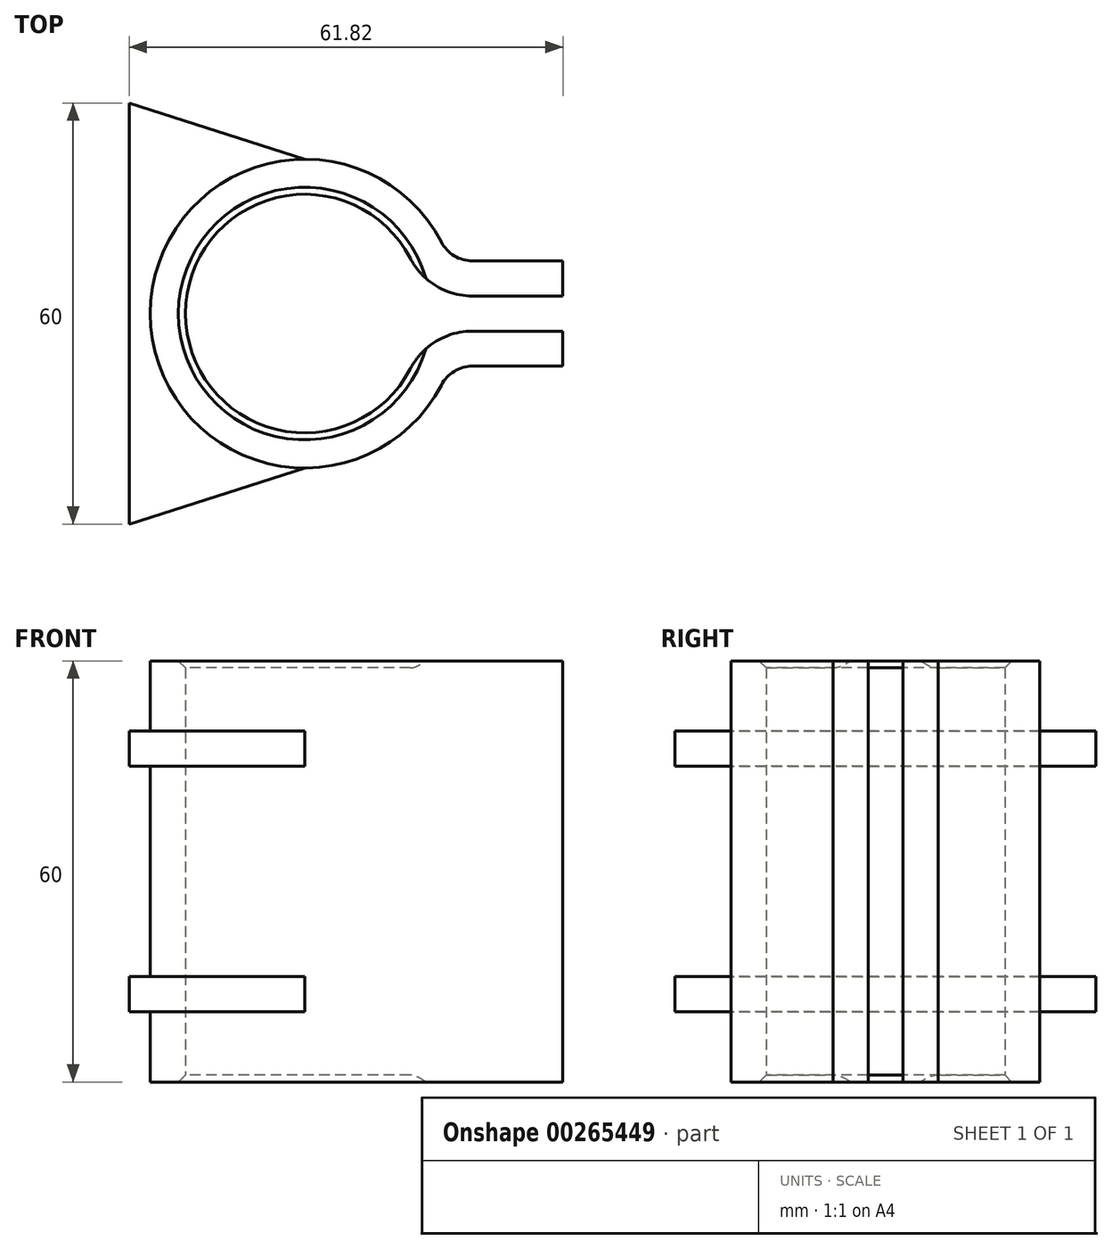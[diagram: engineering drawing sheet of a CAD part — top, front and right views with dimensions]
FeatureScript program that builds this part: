
annotation { "Feature Type Name" : "Feature", "Feature Type Description" : "" }
export const myFeature = defineFeature(function(context is Context, id is Id, definition is map)
    precondition{}
    {
        {
            var Q0;
            Q0=qCreatedBy(makeId("Top.planeOp"),FACE);
            var sketch = newSketch(context, id + "F0", { "sketchPlane" : qUnion([Q0])});
            skArc(sketch, "E0", {"start": v(15.07, 7.87) * mm, "mid": v(-17, 0) * mm, "end": v(15.07, -7.87) * mm});
            skLineSegment(sketch, "E1", {"start": v(23.93, 2.5) * mm, "end": v(36.82, 2.5) * mm});
            skLineSegment(sketch, "E2", {"start": v(-70.72, 0) * mm, "end": v(111.06, 0) * mm, "construction": true});
            skLineSegment(sketch, "E3.MirrorCS", {"start": v(23.93, -2.5) * mm, "end": v(36.82, -2.5) * mm});
            skPoint(sketch, "E4.visualSharp", {"position": v(16.82, 2.5) * mm});
            skArc(sketch, "E4.filletArc", {"start": v(15.07, 7.87) * mm, "mid": v(18.75, 3.95) * mm, "end": v(23.93, 2.5) * mm});
            skPoint(sketch, "E5.visualSharp", {"position": v(16.82, -2.5) * mm});
            skArc(sketch, "E5.filletArc", {"start": v(23.93, -2.5) * mm, "mid": v(18.75, -3.95) * mm, "end": v(15.07, -7.87) * mm});
            skLineSegment(sketch, "E6.0", {"start": v(23.93, -7.5) * mm, "end": v(36.82, -7.5) * mm});
            skArc(sketch, "E6.1", {"start": v(19.5, 10.19) * mm, "mid": v(-22, 0) * mm, "end": v(19.5, -10.19) * mm});
            skLineSegment(sketch, "E6.2", {"start": v(23.93, 7.5) * mm, "end": v(36.82, 7.5) * mm});
            skPoint(sketch, "E7.visualSharp", {"position": v(20.68, -7.5) * mm});
            skArc(sketch, "E7.filletArc", {"start": v(23.93, -7.5) * mm, "mid": v(21.34, -8.22) * mm, "end": v(19.5, -10.19) * mm});
            skPoint(sketch, "E8.visualSharp", {"position": v(20.68, 7.5) * mm});
            skArc(sketch, "E8.filletArc", {"start": v(19.5, 10.19) * mm, "mid": v(21.34, 8.22) * mm, "end": v(23.93, 7.5) * mm});
            skLineSegment(sketch, "E9", {"start": v(36.82, 7.5) * mm, "end": v(36.82, -7.5) * mm, "construction": true});
            skLineSegment(sketch, "E10", {"start": v(36.82, 7.5) * mm, "end": v(36.82, 2.5) * mm});
            skLineSegment(sketch, "E11", {"start": v(36.82, -2.5) * mm, "end": v(36.82, -7.5) * mm});
            skSolve(sketch);
        }
        {
            var Q0;
            Q0=makeQuery(id+"F0.imprint","IMPRINT",FACE,{"disambiguationData":[TD([[makeQuery(id+"F0.imprint","IMPRINT",EDGE,{"derivedFrom":sQuery(id+"F0.wireOp",EDGE,"E0")}),-1.0]])]});
            extrude(context, id + "F1", {"entities" : qUnion([Q0]), "endBound" : BoundingType.SYMMETRIC, "depth" : 60 * mm, "offsetDistance" : 25 * mm});
        }
        {
            var Q0;
            Q0=makeQuery(id+"F1.opExtrude","CAP_EDGE",EDGE,{"disambiguationData":[OSD([sQuery(id+"F0.wireOp",EDGE,"E0")])],"isStart":false});
            var Q1;
            Q1=makeQuery(id+"F1.opExtrude","CAP_EDGE",EDGE,{"disambiguationData":[OSD([sQuery(id+"F0.wireOp",EDGE,"E0")])],"isStart":true});
            chamfer(context, id + "F2", {"entities" : qUnion([Q0, Q1]), "width" : 1 * mm});
        }
        {
            var Q0;
            Q0=makeQuery(id+"F1.opExtrude","CAP_FACE",FACE,{"disambiguationData":[OSD([sQuery(id+"F0.wireOp",EDGE,"E0"),sQuery(id+"F0.wireOp",EDGE,"E1"),sQuery(id+"F0.wireOp",EDGE,"E3.MirrorCS"),sQuery(id+"F0.wireOp",EDGE,"E4.filletArc"),sQuery(id+"F0.wireOp",EDGE,"E5.filletArc"),sQuery(id+"F0.wireOp",EDGE,"E6.0"),sQuery(id+"F0.wireOp",EDGE,"E6.1"),sQuery(id+"F0.wireOp",EDGE,"E6.2"),sQuery(id+"F0.wireOp",EDGE,"E7.filletArc"),sQuery(id+"F0.wireOp",EDGE,"E8.filletArc"),sQuery(id+"F0.wireOp",EDGE,"E10"),sQuery(id+"F0.wireOp",EDGE,"E11")])],"isStart":true});
            var sketch = newSketch(context, id + "F3", { "sketchPlane" : qUnion([Q0])});
            skLineSegment(sketch, "E12", {"start": v(0, 22) * mm, "end": v(-25, 30) * mm});
            skLineSegment(sketch, "E13", {"start": v(-25, 30) * mm, "end": v(-25, -30) * mm});
            skLineSegment(sketch, "E14", {"start": v(-25, -30) * mm, "end": v(0, -22) * mm});
            skLineSegment(sketch, "E15", {"start": v(0, -22) * mm, "end": v(0, 22) * mm, "construction": true});
            skArc(sketch, "E16.0", {"start": v(0, -22) * mm, "mid": v(-22, 0) * mm, "end": v(0, 22) * mm});
            skSolve(sketch);
        }
        {
            var Q0;
            Q0 = qSketchRegion(id + "F3", true);
            extrude(context, id + "F4", {"entities" : qUnion([Q0]), "oppositeDirection" : true, "depth" : 15 * mm, "offsetDistance" : 25 * mm, "hasSecondDirection" : true, "secondDirectionOppositeDirection" : true, "secondDirectionDepth" : 10 * mm});
        }
        {
            var Q0;
            Q0=makeQuery(id+"F4.opExtrude","SWEPT_BODY",BODY,{"disambiguationData":[OSD([sQuery(id+"F3.wireOp",EDGE,"E12"),sQuery(id+"F3.wireOp",EDGE,"E13"),sQuery(id+"F3.wireOp",EDGE,"E14"),sQuery(id+"F3.wireOp",EDGE,"E16.0")])]});
            var Q1;
            Q1=qCreatedBy(makeId("Top.planeOp"),FACE);
            mirror(context, id + "F5", {"operationType" : NewBodyOperationType.ADD, "entities" : qUnion([Q0]), "mirrorPlane" : qUnion([Q1])});
        }
    });
